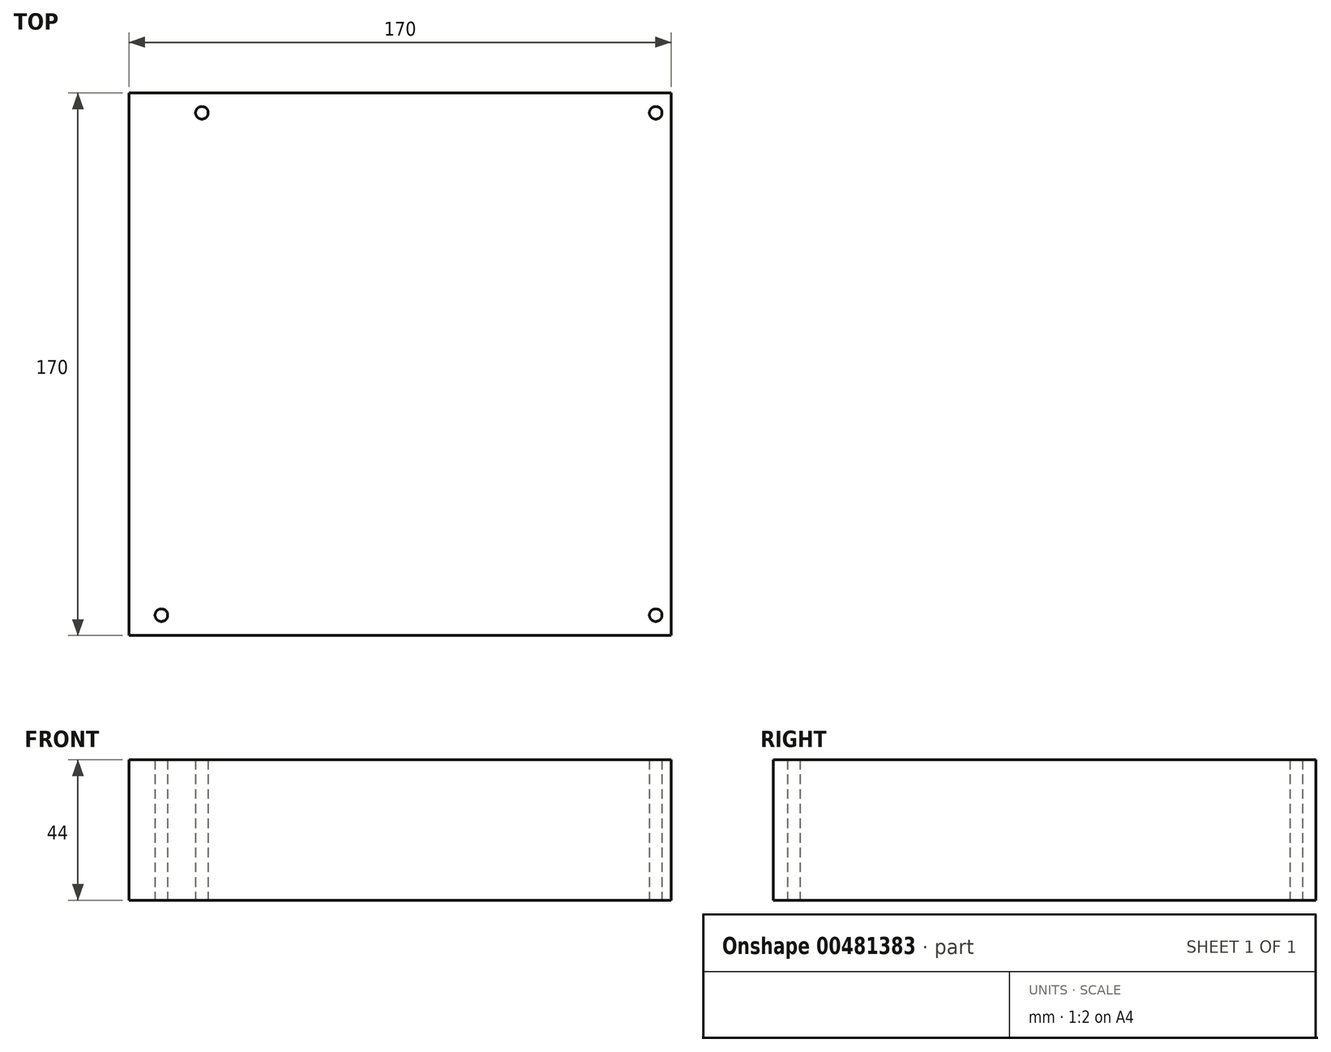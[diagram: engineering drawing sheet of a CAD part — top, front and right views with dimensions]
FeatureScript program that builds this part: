
annotation { "Feature Type Name" : "Feature", "Feature Type Description" : "" }
export const myFeature = defineFeature(function(context is Context, id is Id, definition is map)
    precondition{}
    {
        {
            var Q0;
            Q0=qCreatedBy(makeId("Top.planeOp"),FACE);
            var sketch = newSketch(context, id + "F0", { "sketchPlane" : qUnion([Q0])});
            skLineSegment(sketch, "E0.bottom", {"start": v(170, 170) * mm, "end": v(0, 170) * mm});
            skLineSegment(sketch, "E0.top", {"start": v(170, 0) * mm, "end": v(0, 0) * mm});
            skLineSegment(sketch, "E0.left", {"start": v(170, 170) * mm, "end": v(170, 0) * mm});
            skLineSegment(sketch, "E0.right", {"start": v(0, 170) * mm, "end": v(0, 0) * mm});
            skCircle(sketch, "E1", {"center": v(10.16, 6.35) * mm, "radius": 1.98 * mm});
            skCircle(sketch, "E2", {"center": v(22.86, 163.83) * mm, "radius": 1.98 * mm});
            skCircle(sketch, "E3", {"center": v(165.1, 163.83) * mm, "radius": 1.98 * mm});
            skCircle(sketch, "E4", {"center": v(165.1, 6.35) * mm, "radius": 1.98 * mm});
            skSolve(sketch);
        }
        {
            var Q0;
            Q0=makeQuery(id+"F0.imprint","IMPRINT",FACE,{"disambiguationData":[TD([[makeQuery(id+"F0.imprint","IMPRINT",EDGE,{"derivedFrom":sQuery(id+"F0.wireOp",EDGE,"E0.bottom")}),1.0]])]});
            extrude(context, id + "F1", {"entities" : qUnion([Q0]), "depth" : 44 * mm});
        }
    });
